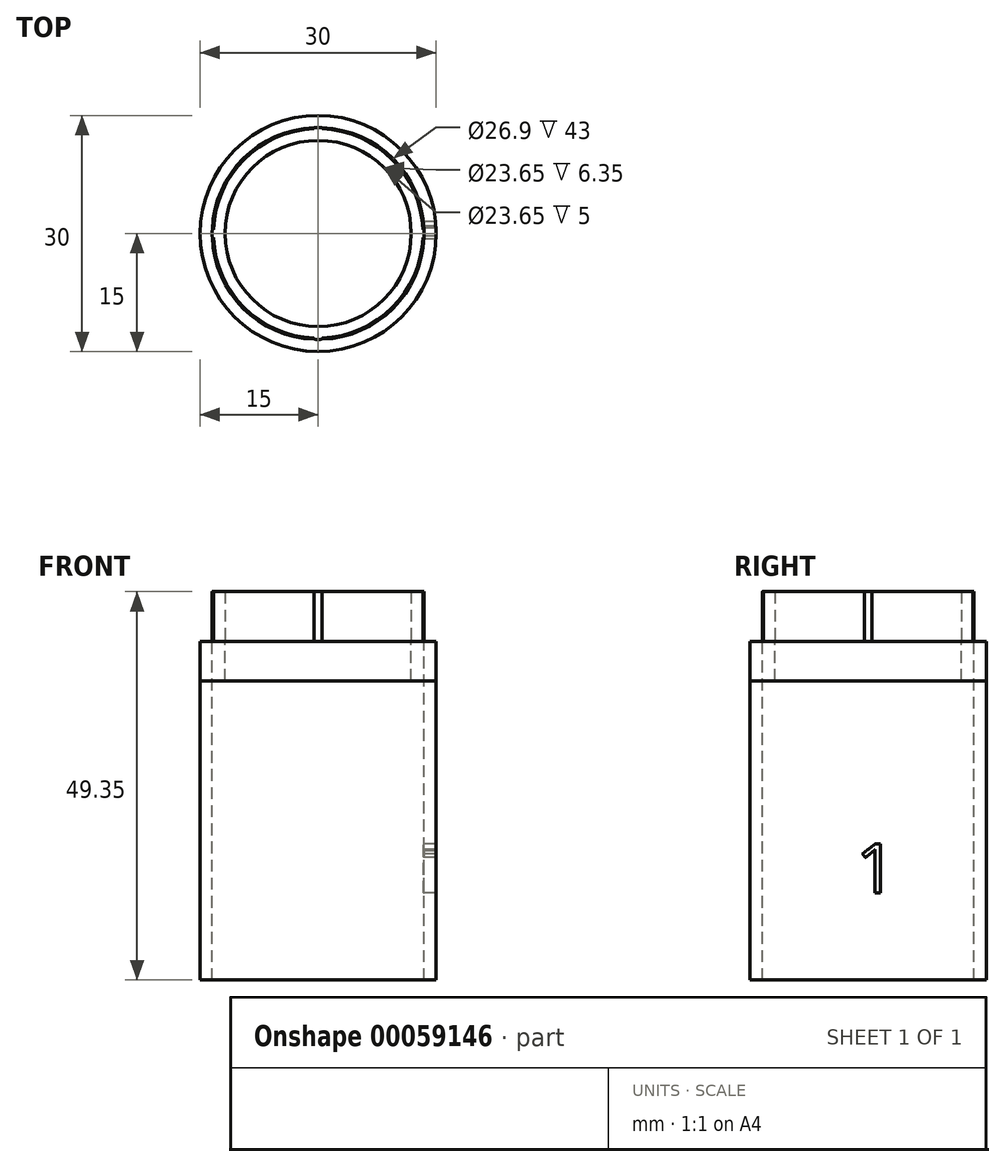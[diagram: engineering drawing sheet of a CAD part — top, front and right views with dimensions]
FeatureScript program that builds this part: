
annotation { "Feature Type Name" : "Feature", "Feature Type Description" : "" }
export const myFeature = defineFeature(function(context is Context, id is Id, definition is map)
    precondition{}
    {
        {
            var Q0;
            Q0=qCreatedBy(makeId("Top.planeOp"),FACE);
            var sketch = newSketch(context, id + "F0", { "sketchPlane" : qUnion([Q0])});
            skCircle(sketch, "E0", {"center": v(0, 0) * mm, "radius": 11.82 * mm});
            skCircle(sketch, "E1", {"center": v(0, 0) * mm, "radius": 13.3 * mm});
            skArc(sketch, "E2", {"start": v(13.44, -0.5) * mm, "mid": v(13.45, 0) * mm, "end": v(13.44, 0.5) * mm});
            skLineSegment(sketch, "E3", {"start": v(13.44, -0.5) * mm, "end": v(13.44, 0) * mm, "construction": true});
            skLineSegment(sketch, "E4", {"start": v(13.44, 0.5) * mm, "end": v(13.44, 0) * mm, "construction": true});
            skLineSegment(sketch, "E5", {"start": v(13.44, 0.5) * mm, "end": v(13.3, 0.5) * mm});
            skLineSegment(sketch, "E6", {"start": v(13.44, -0.5) * mm, "end": v(13.3, -0.5) * mm});
            skArc(sketch, "E7", {"start": v(0.5, 13.44) * mm, "mid": v(0, 13.45) * mm, "end": v(-0.5, 13.44) * mm});
            skLineSegment(sketch, "E8", {"start": v(-0.5, 13.44) * mm, "end": v(0, 13.44) * mm, "construction": true});
            skLineSegment(sketch, "E9", {"start": v(0.5, 13.44) * mm, "end": v(0, 13.44) * mm, "construction": true});
            skLineSegment(sketch, "E10", {"start": v(13.3, 0.5) * mm, "end": v(13.3, 0) * mm, "construction": true});
            skLineSegment(sketch, "E11", {"start": v(0.5, 13.44) * mm, "end": v(0.5, 13.3) * mm});
            skLineSegment(sketch, "E12", {"start": v(-0.5, 13.44) * mm, "end": v(-0.5, 13.3) * mm});
            skArc(sketch, "E13", {"start": v(-13.44, 0.5) * mm, "mid": v(-13.45, 0) * mm, "end": v(-13.44, -0.5) * mm});
            skLineSegment(sketch, "E14", {"start": v(-13.44, 0.5) * mm, "end": v(-13.44, 0) * mm, "construction": true});
            skLineSegment(sketch, "E15", {"start": v(-13.44, 0) * mm, "end": v(-13.44, -0.5) * mm, "construction": true});
            skLineSegment(sketch, "E16", {"start": v(-13.44, 0.5) * mm, "end": v(-13.3, 0.5) * mm});
            skLineSegment(sketch, "E17", {"start": v(-13.44, -0.5) * mm, "end": v(-13.3, -0.5) * mm});
            skArc(sketch, "E18", {"start": v(-0.5, -13.44) * mm, "mid": v(0, -13.45) * mm, "end": v(0.5, -13.44) * mm});
            skLineSegment(sketch, "E19", {"start": v(0.5, -13.44) * mm, "end": v(0, -13.44) * mm, "construction": true});
            skLineSegment(sketch, "E20", {"start": v(0, -13.44) * mm, "end": v(-0.5, -13.44) * mm, "construction": true});
            skLineSegment(sketch, "E21", {"start": v(0.5, -13.44) * mm, "end": v(0.5, -13.3) * mm});
            skLineSegment(sketch, "E22", {"start": v(-0.5, -13.44) * mm, "end": v(-0.5, -13.3) * mm});
            skSolve(sketch);
        }
        {
            var Q0;
            Q0=qSketchRegion(id+"F0",true);
            extrude(context, id + "F1", {"entities" : qUnion([Q0]), "depth" : 6.35 * mm});
        }
        {
            var Q0;
            Q0=qCreatedBy(makeId("Top.planeOp"),FACE);
            var sketch = newSketch(context, id + "F2", { "sketchPlane" : qUnion([Q0])});
            skCircle(sketch, "E23", {"center": v(0, 0) * mm, "radius": 13.45 * mm});
            skCircle(sketch, "E24", {"center": v(0, 0) * mm, "radius": 15 * mm});
            skSolve(sketch);
        }
        {
            var Q0;
            Q0=qSketchRegion(id+"F2",true);
            extrude(context, id + "F3", {"entities" : qUnion([Q0]), "operationType" : NewBodyOperationType.ADD, "oppositeDirection" : true, "depth" : 43 * mm});
        }
        {
            var Q0;
            Q0=qCreatedBy(makeId("Top.planeOp"),FACE);
            var sketch = newSketch(context, id + "F4", { "sketchPlane" : qUnion([Q0])});
            skCircle(sketch, "E25", {"center": v(0, 0) * mm, "radius": 11.82 * mm});
            skCircle(sketch, "E26", {"center": v(0, 0) * mm, "radius": 15 * mm});
            skSolve(sketch);
        }
        {
            var Q0;
            Q0=qSketchRegion(id+"F4",true);
            extrude(context, id + "F5", {"entities" : qUnion([Q0]), "oppositeDirection" : true, "depth" : 5 * mm});
        }
        {
            var Q0;
            Q0=qCreatedBy(makeId("Right.planeOp"),FACE);
            var sketch = newSketch(context, id + "F6", { "sketchPlane" : qUnion([Q0])});
            skText(sketch, "E27", { "text": "1", "fontName": "OpenSans-Regular.ttf"});
            const initialGuessF6  = {"E27": [-0.00152, -0.03192, 1, 0, 0.0063]};
            skSetInitialGuess(sketch, initialGuessF6);
            skSolve(sketch);
        }
        {
            var Q0;
            Q0 = qSketchRegion(id + "F6", true);
            extrude(context, id + "F7", {"entities" : qUnion([Q0]), "operationType" : NewBodyOperationType.REMOVE, "depth" : 25 * mm});
        }
    });
